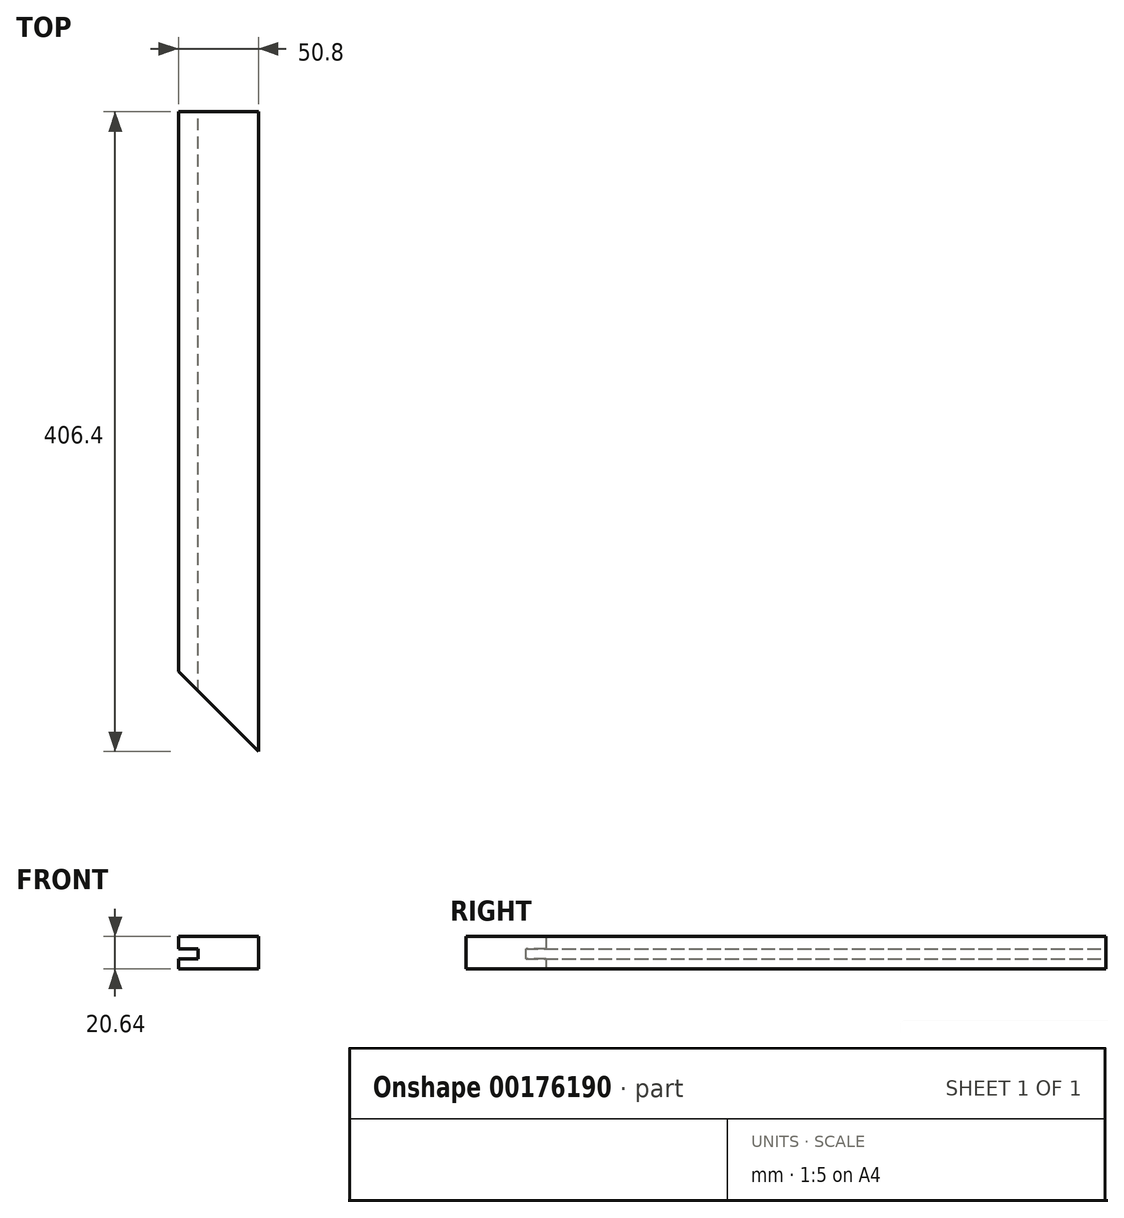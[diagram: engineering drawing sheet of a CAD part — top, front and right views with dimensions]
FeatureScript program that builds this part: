
annotation { "Feature Type Name" : "Feature", "Feature Type Description" : "" }
export const myFeature = defineFeature(function(context is Context, id is Id, definition is map)
    precondition{}
    {
        {
            var Q0;
            Q0=qCreatedBy(makeId("Top.planeOp"),FACE);
            var sketch = newSketch(context, id + "F0", { "sketchPlane" : qUnion([Q0])});
            skLineSegment(sketch, "E0", {"start": v(0, 50.8) * mm, "end": v(0, 406.4) * mm});
            skLineSegment(sketch, "E1", {"start": v(0, 406.4) * mm, "end": v(50.8, 406.4) * mm});
            skLineSegment(sketch, "E2", {"start": v(50.8, 406.4) * mm, "end": v(50.8, 0) * mm});
            skLineSegment(sketch, "E3", {"start": v(50.8, 0) * mm, "end": v(0, 50.8) * mm});
            skSolve(sketch);
        }
        {
            var Q0;
            Q0=makeQuery(id+"F0.imprint","IMPRINT",FACE,{"disambiguationData":[TD([[makeQuery(id+"F0.imprint","IMPRINT",EDGE,{"derivedFrom":sQuery(id+"F0.wireOp",EDGE,"E0")}),-1.0]])]});
            extrude(context, id + "F1", {"entities" : qUnion([Q0]), "depth" : 20.64 * mm});
        }
        {
            var Q0;
            Q0=makeQuery(id+"F1.opExtrude","SWEPT_FACE",FACE,{"disambiguationData":[OSD([sQuery(id+"F0.wireOp",EDGE,"E1")])]});
            var sketch = newSketch(context, id + "F2", { "sketchPlane" : qUnion([Q0])});
            skLineSegment(sketch, "E4.bottom", {"start": v(-12.7, 12.7) * mm, "end": v(0, 12.7) * mm});
            skLineSegment(sketch, "E4.top", {"start": v(-12.7, 6.35) * mm, "end": v(0, 6.35) * mm});
            skLineSegment(sketch, "E4.left", {"start": v(-12.7, 12.7) * mm, "end": v(-12.7, 6.35) * mm});
            skLineSegment(sketch, "E4.right", {"start": v(0, 12.7) * mm, "end": v(0, 6.35) * mm});
            skSolve(sketch);
        }
        {
            var Q0;
            Q0=makeQuery(id+"F2.imprint","IMPRINT",FACE,{"disambiguationData":[TD([[makeQuery(id+"F2.imprint","IMPRINT",EDGE,{"derivedFrom":sQuery(id+"F2.wireOp",EDGE,"E4.bottom")}),-1.0]])]});
            extrude(context, id + "F3", {"entities" : qUnion([Q0]), "operationType" : NewBodyOperationType.REMOVE, "endBound" : BoundingType.THROUGH_ALL, "oppositeDirection" : true, "depth" : 25.4 * mm});
        }
    });
